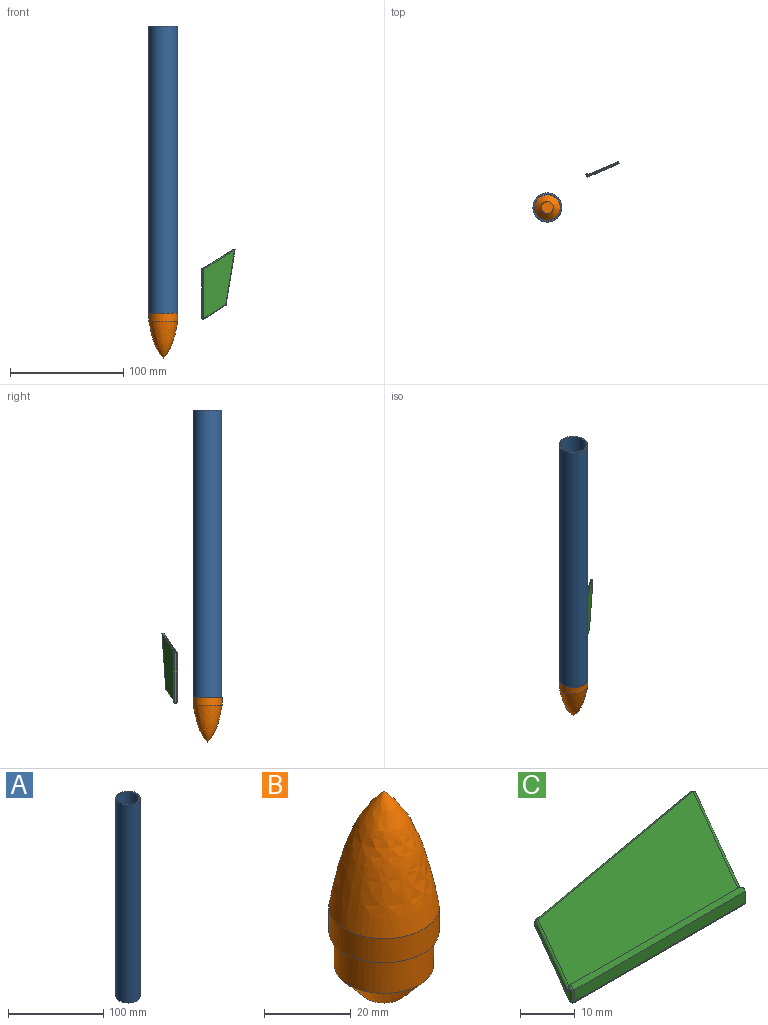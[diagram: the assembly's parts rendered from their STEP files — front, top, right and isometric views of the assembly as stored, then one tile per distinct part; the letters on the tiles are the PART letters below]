
ASSEMBLY  parts=3 mates=1
PART A: 4 faces, bbox 25.4x25.4x254 mm
  f0: cylinder r=11.43mm len=254mm, axis (0,0,-1), area 18241.5mm2, adj f2,f3
  f1: cylinder r=12.7mm len=254mm, axis (0,0,-1), area 20268.3mm2, adj f2,f3
  f2: plane 25.4x25.4mm, normal (0,0,1), area 96.3mm2, adj f0,f1
  f3: plane 25.4x25.4mm, normal (0,0,-1), area 96.3mm2, adj f0,f1
PART B: 7 faces, bbox 25.4x25.4x55.9 mm
  f0: plane 10.72x10.72mm, normal (0,0,-1), area 90.2mm2, adj f3
  f1: plane 25.4x25.4mm, normal (0,0,-1), area 96.3mm2, adj f2,f4
  f2: cylinder r=11.43mm len=22.86mm, axis (0,0,-1), area 683.7mm2, adj f1,f3
  f3: cone r=11.43mm half-angle=40.9deg, axis (0,0,1), area 489.1mm2, adj f0,f2
  f4: cylinder r=12.7mm len=25.4mm, axis (0,0,-1), area 543.4mm2, adj f1,f5
  f5: revolved ~32.54x25.4mm, area 1785.9mm2, adj f4,f6
  f6: plane 0.34x0.34mm, normal (0,0,1), area 0.1mm2, adj f5
PART C: 29 faces, bbox 62.1x30.8x3.2 mm
  f0: plane 21.08x12.17mm, normal (-0.87,0.5,0), area 17.7mm2, adj f8,f12,f13,f16,f19,f20,f23
  f1: plane 29.93x17.28mm, normal (0.87,-0.5,0), area 25.6mm2, adj f3,f4,f15,f22,f26,f27,f28
  f2: plane 48.46x8.55mm, normal (-0.17,0.98,0), area 33.7mm2, adj f13,f14,f21,f22
  f3: plane 43.88x2.57mm, normal (0,-1,0), area 112.6mm2, adj f1,f4,f11,f12
  f4: plane 44.68x1.64mm, normal (0,0,1), area 72.2mm2, adj f1,f3,f6,f12,f16,f28
  f5: plane 60.63x29.62mm, normal (0,0,-1), area 1103.4mm2, adj f8,f11,f14,f15
  f6: plane 43.53x0.67mm, normal (0,1,0), area 28.7mm2, adj f4,f16,f19,f25,f28
  f7: plane 59.68x27.98mm, normal (0,0,1), area 1032.1mm2, adj f20,f21,f25,f26
  f8: cylinder r=0.61mm len=21.38mm, axis (-0.5,-0.87,0), area 23.3mm2, adj f0,f5,f9,f10
  f9: sphere r=0.61mm, area 0.8mm2, adj f8,f11,f12
  f10: sphere r=0.61mm, area 0.3mm2, adj f8,f13,f14
  f11: cylinder r=0.61mm len=43.88mm, axis (1,0,0), area 41.9mm2, adj f3,f5,f9,f15
  f12: cylinder r=0.61mm len=2.57mm, axis (0,0,-1), area 3.1mm2, adj f0,f3,f4,f9,f16
  f13: cylinder r=0.61mm len=0.69mm, axis (0,0,-1), area 0.4mm2, adj f0,f2,f10,f17
  f14: cylinder r=0.61mm len=48.57mm, axis (-0.98,-0.17,0), area 47.1mm2, adj f2,f5,f10,f18
  f15: cylinder r=0.61mm len=30.23mm, axis (0.5,0.87,0), area 33mm2, adj f1,f5,f11,f18
  f16: cylinder r=0.61mm len=1.86mm, axis (0.5,0.87,0), area 1.2mm2, adj f0,f4,f6,f12,f19
  f17: sphere r=0.61mm, area 0.3mm2, adj f13,f20,f21
  f18: sphere r=0.61mm, area 0.8mm2, adj f14,f15,f22
  f19: cylinder r=0.61mm len=0.58mm, axis (0,0,-1), area 0.2mm2, adj f0,f6,f16,f23
  f20: cylinder r=0.61mm len=19.74mm, axis (0.5,0.87,0), area 21.5mm2, adj f0,f7,f17,f23
  f21: cylinder r=0.61mm len=48.57mm, axis (0.98,0.17,0), area 47.1mm2, adj f2,f7,f17,f24
  f22: cylinder r=0.61mm len=0.91mm, axis (0,0,-1), area 0.9mm2, adj f1,f2,f18,f24
  f23: bspline ~1.43x1.35mm, area 1.2mm2, adj f0,f19,f20,f25
  f24: sphere r=0.61mm, area 0.8mm2, adj f21,f22,f26
  f25: cylinder r=0.61mm len=44.23mm, axis (1,0,0), area 41.7mm2, adj f6,f7,f23,f27
  f26: cylinder r=0.61mm len=28.29mm, axis (-0.5,-0.87,0), area 30.9mm2, adj f1,f7,f24,f27
  f27: bspline ~1.63x1.43mm, area 1.6mm2, adj f1,f25,f26,f28
  f28: cylinder r=0.61mm len=0.91mm, axis (0,0,-1), area 0.8mm2, adj f1,f4,f6,f27
PLACE A rot(axis=(1,0.05,0),180deg) t=(-35.22,63.06,452.14)mm
PLACE B rot(axis=(1,0.05,0),180deg) t=(-35.22,63.06,214.67)mm
PLACE C rot(axis=(-0.48,-0.73,-0.48),107.7deg) t=(-0.03,89.77,192.71)mm
MATE fastened B.f4 <-> A.f1  axis (0,0,1) through (-35.22,63.06,198.14)mm
